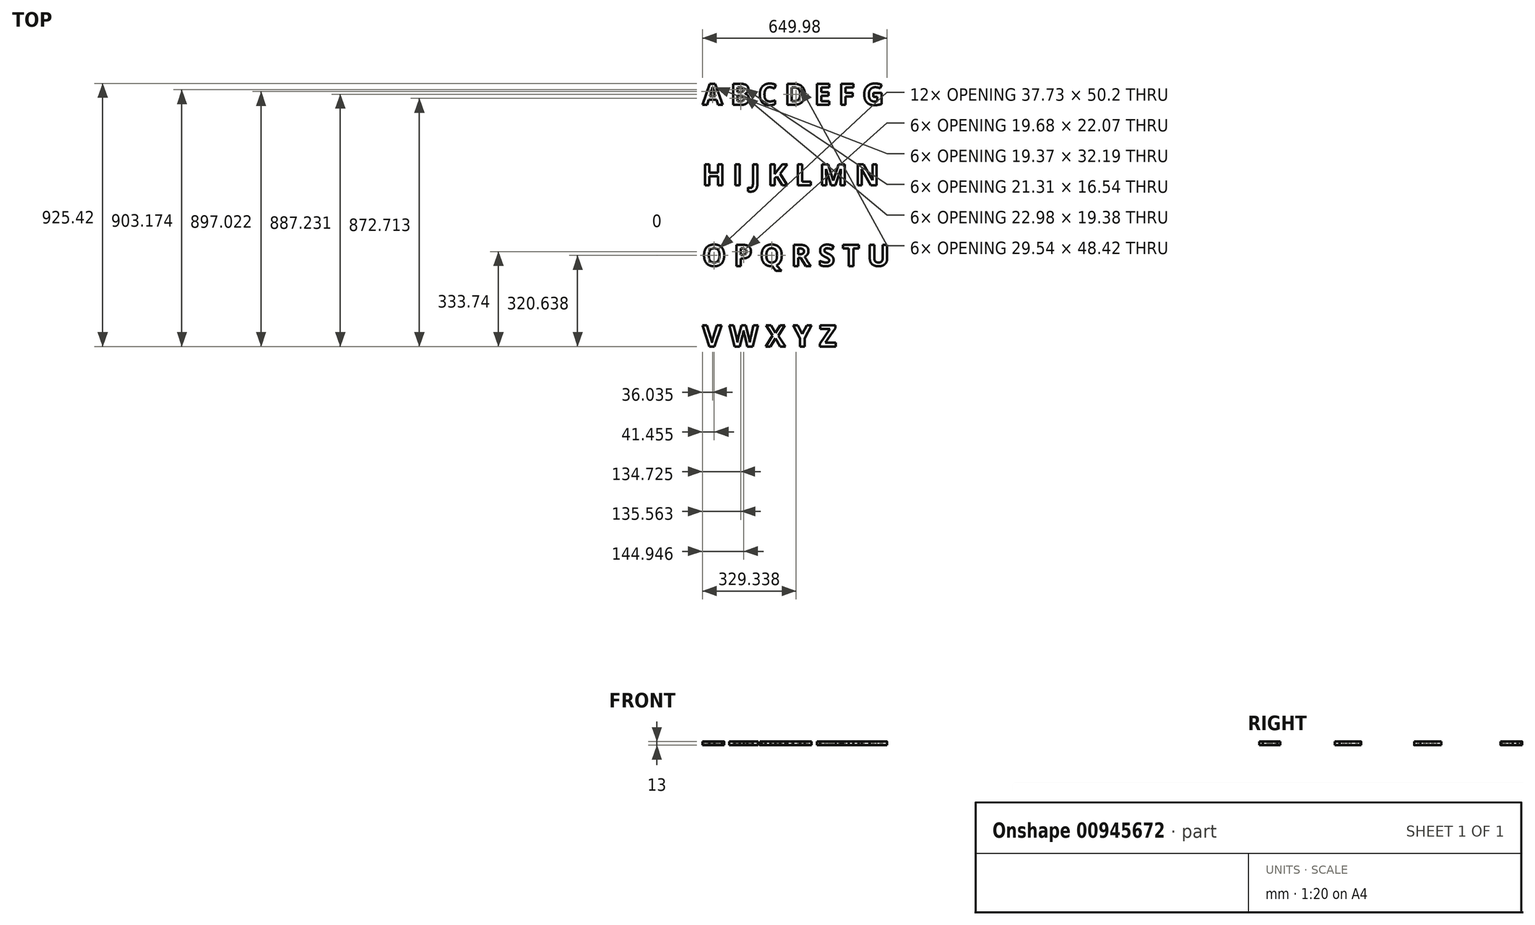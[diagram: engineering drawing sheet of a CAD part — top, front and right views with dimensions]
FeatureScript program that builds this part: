
annotation { "Feature Type Name" : "Feature", "Feature Type Description" : "" }
export const myFeature = defineFeature(function(context is Context, id is Id, definition is map)
    precondition{}
    {
        {
            var Q0;
            Q0=qCreatedBy(makeId("Top.planeOp"),FACE);
            var sketch = newSketch(context, id + "F0", { "sketchPlane" : qUnion([Q0])});
            skText(sketch, "E0", { "text": "A B C D E F G \n\nH I J K L M N\n\nO P Q R S T U\n\nV W X Y Z ", "fontName": "OpenSans-Bold.ttf"});
            const initialGuessF0  = {"E0": [-0.06653, -0.12373, 1, 0, 0.075]};
            skSetInitialGuess(sketch, initialGuessF0);
            skSolve(sketch);
        }
        {
            var Q0;
            Q0=qSketchRegion(id+"F0",true);
            extrude(context, id + "F1", {"entities" : qUnion([Q0]), "oppositeDirection" : true, "depth" : 13 * mm});
        }
    });
